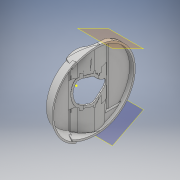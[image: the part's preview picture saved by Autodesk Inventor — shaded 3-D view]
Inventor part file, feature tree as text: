
AUTODESK INVENTOR PART (.ipt)
format: ipt  version: 2018 (Build 220112000, 112)  size: 2,193,920 bytes
history: native  units: mm
features: sketch x65, extrude x59, fillet x18, plane x2, revolve x1, mirror x1
ambient origin geometry x8: Origin, YZ Plane, XZ Plane, XY Plane, X Axis, Y Axis, Z Axis, Center Point
bodies: Solid1 (feature_tree)
feature tree (146):
  extrude  "Extrusion1"  TaperAngle=0.0deg  [1 undecoded]
  extrude  "Extrusion2"  Depth=10.0mm TaperAngle=0.0deg
  extrude  "Extrusion3"  Depth=10.0mm
  extrude  "Extrusion4"  TaperAngle=0.0deg  [1 undecoded]
  extrude  "Extrusion5"  Depth=10.0mm TaperAngle=0.0deg
  sketch  "Sketch6"  dims[d19=10.0mm d20=0.0mm d21=40.0mm]
  extrude  "Extrusion6"  Depth=10.0mm
  extrude  "Extrusion7"  Depth=11.0mm TaperAngle=0.0deg
  extrude  "Extrusion8"  Depth=32.0mm TaperAngle=0.0deg
  extrude  "Extrusion9"  Depth=32.0mm TaperAngle=0.0deg
  extrude  "Extrusion10"  Depth=10.0mm TaperAngle=0.0deg
  extrude  "Extrusion11"  Depth=10.0mm TaperAngle=0.0deg
  extrude  "Extrusion12"  TaperAngle=0.0deg  [1 undecoded]
  extrude  "Extrusion14"  Depth=48.3mm
  extrude  "Extrusion15"  TaperAngle=0.0deg  [1 undecoded]
  extrude  "Extrusion16"  Depth=10.0mm TaperAngle=0.0deg
  extrude  "Extrusion17"  Depth=11.63mm TaperAngle=0.0deg
  sketch  "Sketch21"  dims[d83=0.0mm d84=0.0mm d85=0.0mm d86=0.0mm]
  extrude  "Extrusion19"  Depth=11.63mm TaperAngle=0.0deg
  extrude  "Extrusion20"  TaperAngle=0.0deg  [1 undecoded]
  extrude  "Extrusion21"  Depth=10.0mm TaperAngle=0.0deg
  extrude  "Extrusion22"  TaperAngle=0.0deg  [1 undecoded]
  extrude  "Extrusion23"  Depth=2.86mm TaperAngle=0.0deg
  extrude  "Extrusion24"  Depth=2.01mm
  extrude  "Extrusion25"  Depth=10.0mm TaperAngle=0.0deg
  sketch  "Sketch33"  dims[d115=7.8mm d116=0.0mm d117=0.0mm d118=0.0mm]
  extrude  "Extrusion26"  Depth=10.0mm TaperAngle=0.0deg
  extrude  "Extrusion27"  TaperAngle=0.0deg  [1 undecoded]
  extrude  "Extrusion28"  Depth=22.0mm TaperAngle=0.0deg
  extrude  "Extrusion29"  Depth=17.0mm TaperAngle=0.0deg
  extrude  "Extrusion30"  Depth=2.0mm
  extrude  "Extrusion31"  Depth=2.0mm TaperAngle=0.0deg
  extrude  "Extrusion32"  Depth=18.0mm TaperAngle=0.0deg
  extrude  "Extrusion33"  Depth=1.02mm
  sketch  "Sketch42"  dims[d151=2.0mm d152=2.0mm]
  extrude  "Extrusion34"  Depth=7.72mm TaperAngle=0.0deg
  extrude  "Extrusion36"  Depth=2.0mm
  extrude  "Extrusion37"  Depth=2.0mm
  revolve  "Revolution3"  [1 undecoded]
  extrude  "Extrusion38"  Depth=2.0mm
  extrude  "Extrusion39"  Depth=10.0mm TaperAngle=0.0deg
  fillet  "Fillet1"  Radius=7.83mm
  fillet  "Fillet2"  Radius=20.0mm
  sketch  "Sketch51"  dims[d171=2.0mm d172=2.0mm]
  extrude  "Extrusion41"  Depth=6.4mm TaperAngle=0.0deg
  mirror  "Mirror1"
  extrude  "Extrusion42"  Depth=2.0mm
  sketch  "Sketch54"
  sketch  "Sketch55"
  sketch  "Sketch56"
  extrude  "Extrusion44"  Depth=2.0mm
  extrude  "Extrusion45"  Depth=2.0mm
  extrude  "Extrusion46"  [1 undecoded]
  extrude  "Extrusion47"  [1 undecoded]
  plane  "Work Plane2"
  extrude  "Extrusion48"  [1 undecoded]
  extrude  "Extrusion49"  [1 undecoded]
  plane  "Work Plane5"
  extrude  "Extrusion50"  [1 undecoded]
  extrude  "Extrusion51"  [1 undecoded]
  fillet  "Fillet3"  [1 undecoded]
  fillet  "Fillet4"  [1 undecoded]
  extrude  "Extrusion52"  [1 undecoded]
  extrude  "Extrusion53"  [1 undecoded]
  extrude  "Extrusion54"  [1 undecoded]
  extrude  "Extrusion55"  [1 undecoded]
  fillet  "Fillet5"  [1 undecoded]
  extrude  "Extrusion57"  [1 undecoded]
  extrude  "Extrusion58"  [1 undecoded]
  extrude  "Extrusion59"  [1 undecoded]
  fillet  "Fillet7"  [1 undecoded]
  fillet  "Fillet8"  [1 undecoded]
  fillet  "Fillet9"  [1 undecoded]
  fillet  "Fillet10"  [1 undecoded]
  fillet  "Fillet11"  [1 undecoded]
  fillet  "Fillet12"  [1 undecoded]
  fillet  "Fillet13"  [1 undecoded]
  fillet  "Fillet14"  [1 undecoded]
  extrude  "Extrusion60"  [1 undecoded]
  extrude  "Extrusion61"  [1 undecoded]
  extrude  "Extrusion62"  [1 undecoded]
  extrude  "Extrusion63"  [1 undecoded]
  extrude  "Extrusion64"  [1 undecoded]
  extrude  "Extrusion65"  [1 undecoded]
  fillet  "Fillet15"  [1 undecoded]
  fillet  "Fillet16"  [1 undecoded]
  fillet  "Fillet17"  [1 undecoded]
  fillet  "Fillet18"  [1 undecoded]
  fillet  "Fillet19"  [1 undecoded]
  sketch  "Sketch1"  dims[d0=10.0mm d1=0.0mm d2=0.0mm d3=0.0mm]
  sketch  "Sketch2"  dims[d4=0.0mm d5=0.0mm d6=10.0mm d7=0.0mm]
  sketch  "Sketch3"  dims[d8=10.0mm d9=0.0mm d10=50.0mm]
  sketch  "Sketch4"  dims[d11=10.0mm d12=0.0mm d13=0.0mm d14=0.0mm]
  sketch  "Sketch5"  dims[d15=0.0mm d16=0.0mm d17=10.0mm d18=0.0mm]
  sketch  "Sketch7"  dims[d22=38.0mm d23=11.0mm d24=0.0mm]
  sketch  "Sketch8"  dims[d25=9.5mm d26=0.0mm d33=32.0mm d34=0.0mm]
  sketch  "Sketch9"  dims[d37=32.0mm d38=0.0mm d39=32.0mm d40=0.0mm]
  sketch  "Sketch10"  dims[d41=32.0mm d42=0.0mm d45=10.0mm d46=0.0mm]
  sketch  "Sketch11"  dims[d47=10.0mm d48=0.0mm d49=10.0mm d50=0.0mm]
  sketch  "Sketch12"  dims[d51=0.0mm d52=0.0mm d53=0.0mm d54=0.0mm]
  sketch  "Sketch13"  dims[d65=46.0mm d66=48.3mm]
  sketch  "Sketch16"  dims[d67=9.0mm d68=0.0mm d69=0.0mm d70=0.0mm]
  sketch  "Sketch18"  dims[d71=0.0mm d72=0.0mm d73=10.0mm d74=0.0mm]
  sketch  "Sketch19"  dims[d75=5.0mm d76=0.0mm d77=11.63mm d78=0.0mm]
  sketch  "Sketch20"  dims[d79=11.63mm d80=0.0mm d81=11.63mm d82=0.0mm]
  sketch  "Sketch22"  dims[d87=30.0mm d88=10.0mm d89=0.0mm]
  sketch  "Sketch23"  dims[d92=10.0mm d93=0.0mm d94=0.0mm d95=0.0mm]
  sketch  "Sketch24"  dims[d96=135.0deg d99=2.86mm d100=0.0mm]
  sketch  "Sketch25"  dims[d101=0.0mm d102=0.0mm d105=2.01mm]
  sketch  "Sketch31"  dims[d106=2.22mm d107=10.0mm d108=0.0mm]
  sketch  "Sketch32"  dims[d109=10.0mm d110=0.0mm d113=7.8mm d114=0.0mm]
  sketch  "Sketch34"  dims[d119=16.0mm d120=0.0mm d121=22.0mm d122=0.0mm]
  sketch  "Sketch35"  dims[d123=22.0mm d124=0.0mm d126=17.0mm d127=0.0mm]
  sketch  "Sketch36"  dims[d128=17.0mm d129=0.0mm d130=2.0mm]
  sketch  "Sketch37"  dims[d131=2.0mm d132=6.95mm d133=0.0mm]
  sketch  "Sketch38"  dims[d134=6.95mm d135=0.0mm d136=18.0mm d137=0.0mm]
  sketch  "Sketch39"  dims[d138=16.0mm d139=0.0mm d140=1.02mm]
  sketch  "Sketch40"  dims[d143=15.5mm d144=0.0mm d146=7.72mm d147=0.0mm]
  sketch  "Sketch41"  dims[d148=17.0mm d149=0.0mm d150=2.0mm]
  sketch  "Sketch43"  dims[d153=2.0mm d154=2.0mm]
  sketch  "Sketch45"  dims[d155=2.0mm d156=2.0mm]
  sketch  "Sketch47"  dims[d157=2.0mm d158=10.0mm d159=0.0mm d160=7.83mm d161=0.0mm d162=20.0mm d163=0.0mm]
  sketch  "Sketch48"  dims[d164=0.0mm d165=0.0mm d166=6.4mm d167=0.0mm]
  sketch  "Sketch49"  dims[d168=6.14mm d169=0.0mm d170=2.0mm]
  sketch  "Sketch52"  dims[d173=2.0mm d174=2.0mm]
  sketch  "Sketch53"
  sketch  "Sketch57"
  sketch  "Sketch60"
  sketch  "Sketch61"
  sketch  "Sketch62"
  sketch  "Sketch63"
  sketch  "Sketch65"
  sketch  "Sketch66"
  sketch  "Sketch67"
  sketch  "Sketch68"
  sketch  "Sketch69"
  sketch  "Sketch70"
  sketch  "Sketch72"
  sketch  "Sketch73"
  sketch  "Sketch74"
  sketch  "Sketch75"
  sketch  "Sketch76"
  sketch  "Sketch78"
  sketch  "Sketch80"
  sketch  "Sketch81"
  sketch  "Sketch82"
note: 43 required parameter values undecoded (feature->parameter linkage not recoverable at this tier; creation-order binding heuristic only, values carry confidence <= 0.55)